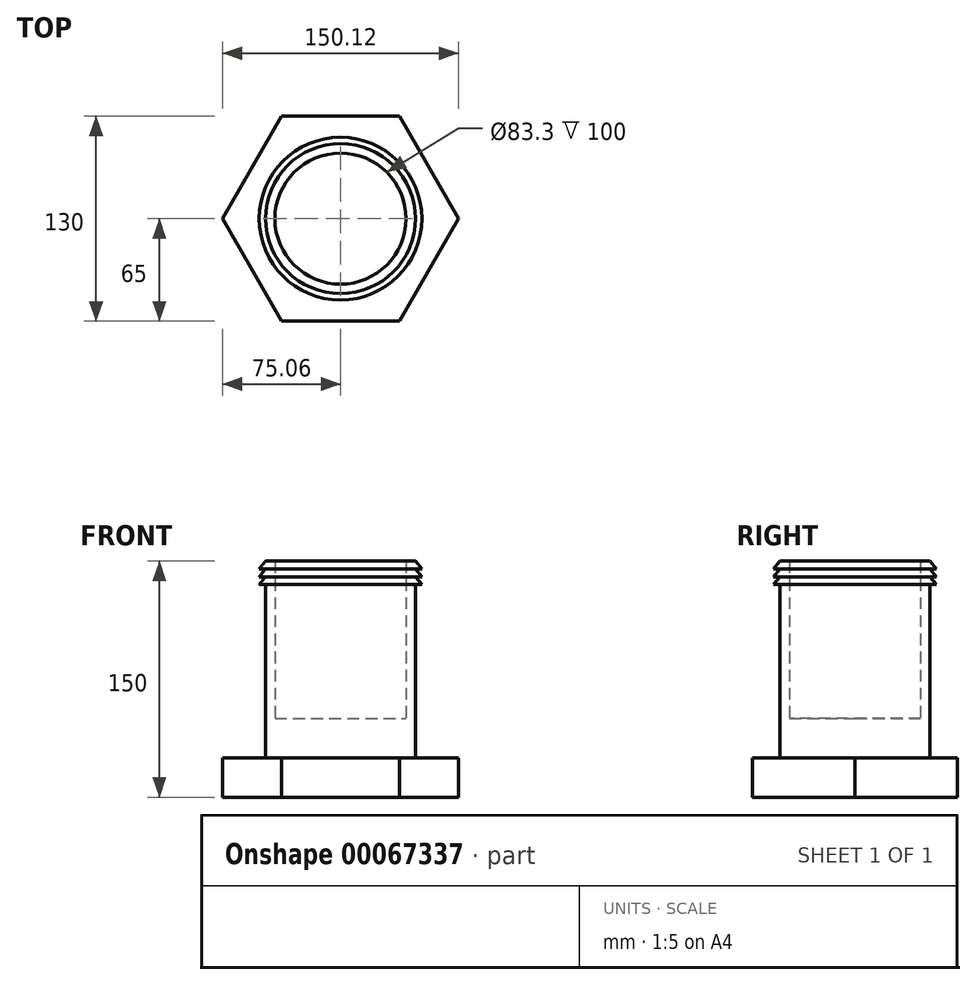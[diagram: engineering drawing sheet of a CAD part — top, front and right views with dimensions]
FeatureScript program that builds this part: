
annotation { "Feature Type Name" : "Feature", "Feature Type Description" : "" }
export const myFeature = defineFeature(function(context is Context, id is Id, definition is map)
    precondition{}
    {
        {
            var Q0;
            Q0=qCreatedBy(makeId("Top.planeOp"),FACE);
            var sketch = newSketch(context, id + "F0", { "sketchPlane" : qUnion([Q0])});
            skCircle(sketch, "E0", {"center": v(0, 0) * mm, "radius": 47.65 * mm});
            skSolve(sketch);
        }
        {
            var Q0;
            Q0=makeQuery(id+"F0.imprint","IMPRINT",FACE,{"disambiguationData":[TD([[makeQuery(id+"F0.imprint","IMPRINT",EDGE,{"derivedFrom":sQuery(id+"F0.wireOp",EDGE,"E0")}),1.0]])]});
            extrude(context, id + "F1", {"entities" : qUnion([Q0]), "depth" : 50 * mm});
        }
        {
            var Q0;
            Q0=qCreatedBy(makeId("Right.planeOp"),FACE);
            var sketch = newSketch(context, id + "F2", { "sketchPlane" : qUnion([Q0])});
            skLineSegment(sketch, "E1", {"start": v(41.65, 50) * mm, "end": v(41.65, 150) * mm});
            skLineSegment(sketch, "E2", {"start": v(41.65, 150) * mm, "end": v(47.65, 150) * mm});
            skLineSegment(sketch, "E3", {"start": v(47.65, 150) * mm, "end": v(51.65, 145) * mm});
            skLineSegment(sketch, "E4", {"start": v(51.65, 145) * mm, "end": v(47.65, 145) * mm});
            skLineSegment(sketch, "E5", {"start": v(47.65, 145) * mm, "end": v(51.65, 140) * mm});
            skLineSegment(sketch, "E6", {"start": v(51.65, 140) * mm, "end": v(47.65, 140) * mm});
            skLineSegment(sketch, "E7", {"start": v(47.65, 140) * mm, "end": v(51.65, 135) * mm});
            skLineSegment(sketch, "E8", {"start": v(51.65, 135) * mm, "end": v(47.65, 135) * mm});
            skLineSegment(sketch, "E9", {"start": v(47.65, 135) * mm, "end": v(47.65, 50) * mm});
            skLineSegment(sketch, "E10", {"start": v(47.65, 50) * mm, "end": v(41.65, 50) * mm});
            skLineSegment(sketch, "E11", {"start": v(0, 0) * mm, "end": v(0, 218.75) * mm, "construction": true});
            skSolve(sketch);
        }
        {
            var Q0;
            Q0 = qSketchRegion(id + "F2", true);
            var Q1;
            Q1=sQuery(id+"F2.wireOp",EDGE,"E11");
            revolve(context, id + "F3", {"operationType" : NewBodyOperationType.ADD, "entities" : qUnion([Q0]), "axis" : qUnion([Q1]), "revolveType" : RevolveType.FULL});
        }
        {
            var Q0;
            Q0=makeQuery(id+"F1.opExtrude","CAP_FACE",FACE,{"disambiguationData":[OSD([sQuery(id+"F0.wireOp",EDGE,"E0")])],"isStart":true});
            var sketch = newSketch(context, id + "F4", { "sketchPlane" : qUnion([Q0])});
            skSolve(sketch);
        }
        {
            var Q0;
            Q0=makeQuery(id+"F4.imprint","IMPRINT",FACE,{"disambiguationData":[TD([[makeQuery(id+"F4.imprint","IMPRINT",EDGE,{"derivedFrom":makeQuery(id+"F1.opExtrude","CAP_EDGE",EDGE,{"disambiguationData":[OSD([sQuery(id+"F0.wireOp",EDGE,"E0")])],"isStart":true})}),-1.0]])]});
            var sketch = newSketch(context, id + "F5", { "sketchPlane" : qUnion([Q0])});
            skCircle(sketch, "E12.cCircle", {"center": v(0, 0) * mm, "radius": 65 * mm, "construction": true});
            skLineSegment(sketch, "E12.0", {"start": v(75.06, 0) * mm, "end": v(37.53, -65) * mm});
            skLineSegment(sketch, "E12.1", {"start": v(37.53, -65) * mm, "end": v(-37.53, -65) * mm});
            skLineSegment(sketch, "E12.2", {"start": v(-37.53, -65) * mm, "end": v(-75.06, 0) * mm});
            skLineSegment(sketch, "E12.3", {"start": v(-75.06, 0) * mm, "end": v(-37.53, 65) * mm});
            skLineSegment(sketch, "E12.4", {"start": v(-37.53, 65) * mm, "end": v(37.53, 65) * mm});
            skLineSegment(sketch, "E12.5", {"start": v(37.53, 65) * mm, "end": v(75.06, 0) * mm});
            skPoint(sketch, "E12.0.midPoint", {"position": v(56.3, -32.5) * mm});
            skSolve(sketch);
        }
        {
            var Q0;
            Q0 = qSketchRegion(id + "F5", true);
            extrude(context, id + "F6", {"entities" : qUnion([Q0]), "operationType" : NewBodyOperationType.ADD, "oppositeDirection" : true, "depth" : 25 * mm});
        }
    });
